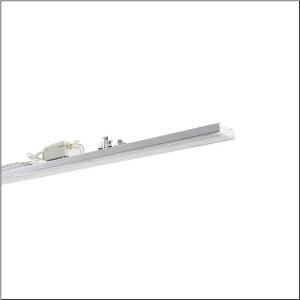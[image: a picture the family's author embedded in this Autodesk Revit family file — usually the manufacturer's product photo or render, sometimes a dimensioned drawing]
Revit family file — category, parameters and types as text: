
# Revit family: licross_r__21_recessed_mo_52tl11de45xg_1e96
name_source: partatom
category: Lighting Fixtures
units: mm (PartAtom-declared; Revit-internal decimal feet)

## family parameters
Cut with Voids When Loaded = No
Host = Face
Light Source = No
Part Type = Normal
Room Calculation Point = No
Round Connector Dimension = Use Diameter
Shared = No

## types (1)
- --- (1 x LED, 5060 lm, 29.9 W, 4000K)
    Apparent Load = 30 VA
    CIE Flux Codes = 89 96 99 100 100
    Color Rendering = 80
    Color Temperature = 4000K
    Default Elevation = 1800 mm
    Description = Licross® 21 Recessed MO, luminaire insert, of sheet steel, galvanised, coil coated, white, length: 750mm, width: 66mm, height: 67mm, LED rated luminous flux: 5.060lm, light colour: 840, control gear: DALI 2, with plug, 5-pole, with phase selection, mains connection: 220..240V, AC, 50/60Hz, rated input power: 30W, halogen-free wiring, primary light control with lens, of plastic, primary optical cover: cover, of PMMA, light emission: direct distribution, primary light characteristic: symmetric, protection rating (complete): IP40, insulation class (complete): insulation class I (protective earthing), certification: CE, ENEC, VDE, UKCA, protection symbol: D if used in an environment without relevant dust loads with corresponding accessories, impact resistance: IK06, permissible ambient temperature for indoor applications: -25..+35°C, corresponds to IFS (International Featured Standards) requirements for safety and quality in the food industry, reducing of maximum allowable ambient temperature of 5°C with ceiling mounting, LABS conformity tested according to VDMA 24364:2018-05, packaging unit: 1 piece
    Height = 58 mm
    Lamp = 1 x LED
    Lamp Light Flux = 5060 lm
    Lamp Power = 29.9 W
    Lamp count = 1
    Length = 750 mm
    Luminous efficacy = 169 lm/W
    Manufacturer = Siteco
    ModVariant = No
    Model = 52TL11DE45XG
    Mounting Place = Ceiling
    Mounting Type = Pendant
    Number of Poles = 1
    OnlyDefault = Yes
    Power Factor = 1
    Product Name = Licross® 21 Recessed MO
    Product group = luminaire insert
    ProductGroupID = 901
    Protection Class = Protection class I
    Protection Degree = IP 40
    RLX_Detail_Level = 1
    RLX_Emergency_Light_Flux = 0 lm
    RLX_Emergency_Type = 0
    RLX_Emergency_Type_DB = No
    RlxData = <blob elided: 28749 chars, md5=17c127dd>
    Socket = socket
    Standby Power = 0 W
    System Light Flux = 5060 lm
    System Power = 30 W
    Type Comments = factory setting: luminous flux: 100 % | dim-lin: 254 | 390 mA
    Type Image = l_1296930.jpg
    URL = http://relux.com
    VarID = @adj_058745
    Voltage = 0 V
    Weight = 0.00 kg
    Width = 66 mm

## geometry (parser evidence)
native form markers: Blend x4, Sweep x9
no freeform markers — native parametric forms only
